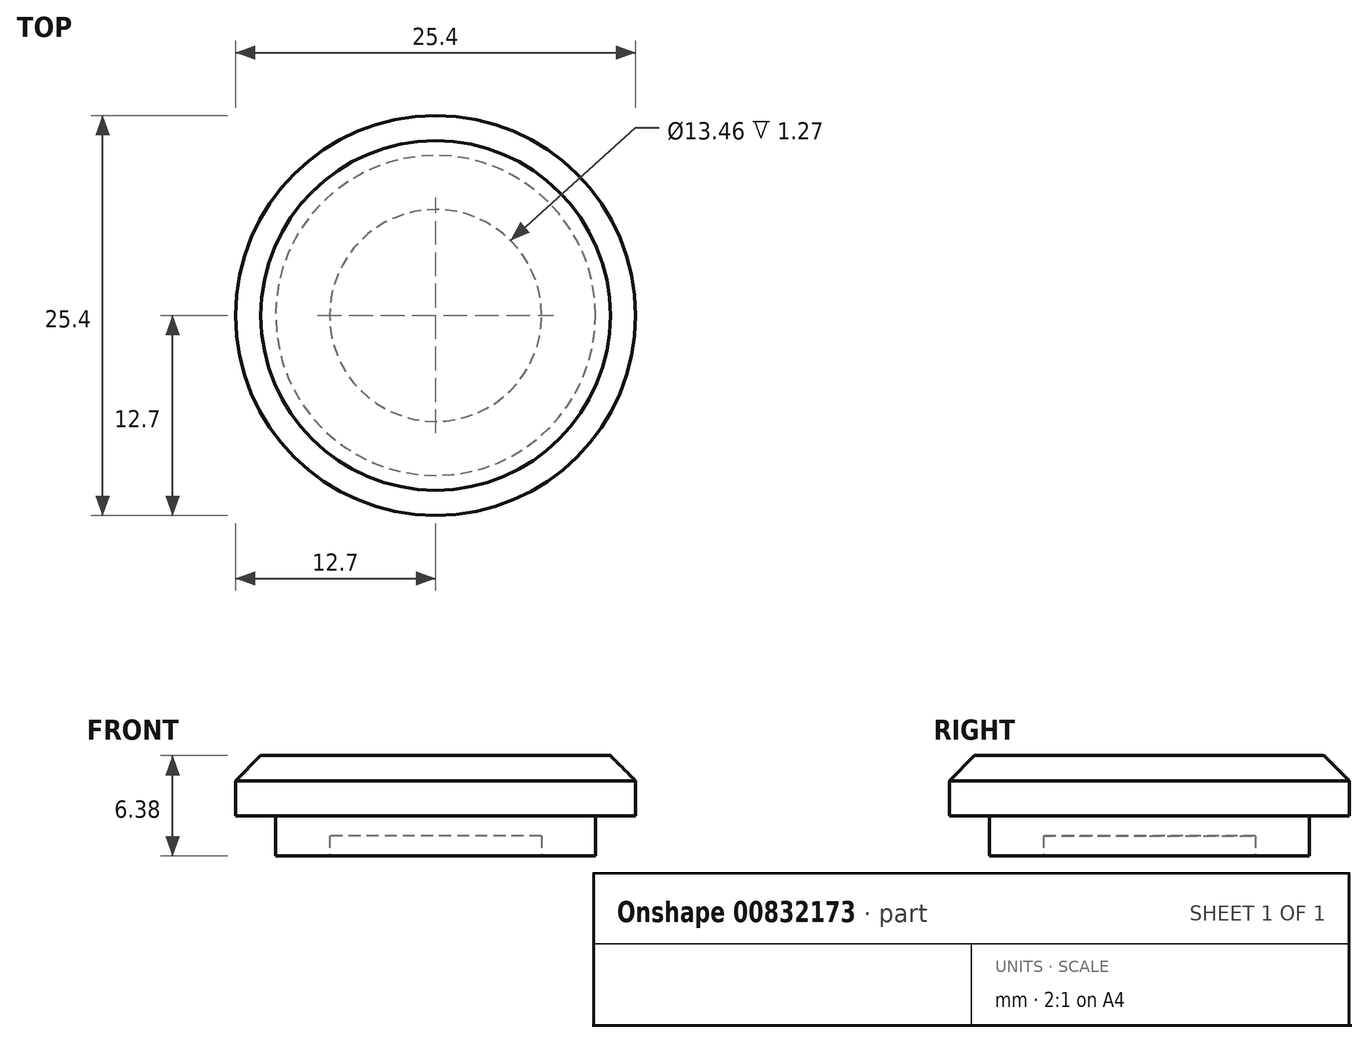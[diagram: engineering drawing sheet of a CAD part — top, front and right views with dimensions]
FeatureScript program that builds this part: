
annotation { "Feature Type Name" : "Feature", "Feature Type Description" : "" }
export const myFeature = defineFeature(function(context is Context, id is Id, definition is map)
    precondition{}
    {
        {
            var Q0;
            Q0=qCreatedBy(makeId("Top.planeOp"),FACE);
            var sketch = newSketch(context, id + "F0", { "sketchPlane" : qUnion([Q0])});
            skCircle(sketch, "E0", {"center": v(0, 0) * mm, "radius": 12.7 * mm});
            skCircle(sketch, "E1", {"center": v(0, 0) * mm, "radius": 10.16 * mm});
            skCircle(sketch, "E2", {"center": v(0, 0) * mm, "radius": 6.73 * mm});
            skSolve(sketch);
        }
        {
            var Q0;
            Q0=makeQuery(id+"F0.imprint","IMPRINT",FACE,{"disambiguationData":[TD([[makeQuery(id+"F0.imprint","IMPRINT",EDGE,{"derivedFrom":sQuery(id+"F0.wireOp",EDGE,"E2")}),1.0]])]});
            var Q1;
            Q1=makeQuery(id+"F0.imprint","IMPRINT",FACE,{"disambiguationData":[TD([[makeQuery(id+"F0.imprint","IMPRINT",EDGE,{"derivedFrom":sQuery(id+"F0.wireOp",EDGE,"E1")}),1.0]])]});
            var Q2;
            Q2=makeQuery(id+"F0.imprint","IMPRINT",FACE,{"disambiguationData":[TD([[makeQuery(id+"F0.imprint","IMPRINT",EDGE,{"derivedFrom":sQuery(id+"F0.wireOp",EDGE,"E0")}),1.0]])]});
            extrude(context, id + "F1", {"entities" : qUnion([Q0, Q1, Q2]), "depth" : 6.38 * mm, "offsetDistance" : 25.4 * mm});
        }
        {
            var Q0;
            Q0=makeQuery(id+"F0.imprint","IMPRINT",FACE,{"disambiguationData":[TD([[makeQuery(id+"F0.imprint","IMPRINT",EDGE,{"derivedFrom":sQuery(id+"F0.wireOp",EDGE,"E0")}),1.0]])]});
            extrude(context, id + "F2", {"entities" : qUnion([Q0]), "operationType" : NewBodyOperationType.REMOVE, "oppositeDirection" : true, "depth" : -2.54 * mm, "offsetDistance" : 25.4 * mm});
        }
        {
            var Q0;
            Q0=makeQuery(id+"F0.imprint","IMPRINT",FACE,{"disambiguationData":[TD([[makeQuery(id+"F0.imprint","IMPRINT",EDGE,{"derivedFrom":sQuery(id+"F0.wireOp",EDGE,"E2")}),1.0]])]});
            extrude(context, id + "F3", {"entities" : qUnion([Q0]), "operationType" : NewBodyOperationType.REMOVE, "oppositeDirection" : true, "depth" : -1.27 * mm, "offsetDistance" : 25.4 * mm});
        }
        {
            var Q0;
            Q0=makeQuery(id+"F1.opExtrude","CAP_EDGE",EDGE,{"disambiguationData":[OSD([sQuery(id+"F0.wireOp",EDGE,"E0")])],"isStart":false});
            chamfer(context, id + "F4", {"entities" : qUnion([Q0]), "width" : 1.6 * mm, "tangentPropagation" : true});
        }
    });
